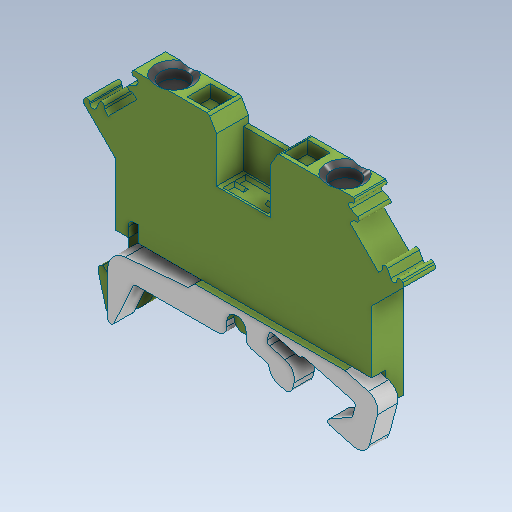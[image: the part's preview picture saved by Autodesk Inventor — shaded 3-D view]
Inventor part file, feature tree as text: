
AUTODESK INVENTOR PART (.ipt)
format: ipt  version: 2025.2 (Build 292293000, 293)  size: 846,336 bytes
history: native  units: mm
features: other x130, sketch x12, extrude x10, hole x2
ambient origin geometry x8: Origin, YZ Plane, XZ Plane, XY Plane, X Axis, Y Axis, Z Axis, Center Point
bodies: Solid1 (feature_tree)
feature tree (154):
  extrude  "Extrusion1"  Depth=2.1mm TaperAngle=0.0deg
  extrude  "Extrusion2"  Depth=2.0mm TaperAngle=0.0deg
  extrude  "Extrusion3"  Depth=7.0mm TaperAngle=0.0deg
  extrude  "Extrusion4"  Depth=5.0mm TaperAngle=0.0deg
  extrude  "Extrusion5"  Depth=3.6mm TaperAngle=0.0deg
  extrude  "Extrusion6"  TaperAngle=0.0deg  [1 undecoded]
  extrude  "Extrusion7"  TaperAngle=0.0deg  [1 undecoded]
  extrude  "Extrusion8"  TaperAngle=0.0deg  [1 undecoded]
  hole  "Hole1"  [1 undecoded]
  hole  "Hole2"  [1 undecoded]
  extrude  "Extrusion9"  Depth=10.0mm
  extrude  "Extrusion10"  Depth=10.0mm
  other  "1_2_XY"
  other  "1_2_YZ"
  other  "1_2_ZX"
  other  "1_2_X"
  other  "1_2_Y"
  other  "1_2_Z"
  other  "1_2_Center"
  other  "1_3_XY"
  other  "1_3_YZ"
  other  "1_3_ZX"
  other  "1_3_X"
  other  "1_3_Y"
  other  "1_3_Z"
  other  "1_3_Center"
  other  "1_4_XY"
  other  "1_4_YZ"
  other  "1_4_ZX"
  other  "1_4_X"
  other  "1_4_Y"
  other  "1_4_Z"
  other  "1_4_Center"
  other  "1_5_XY"
  other  "1_5_YZ"
  other  "1_5_ZX"
  other  "1_5_X"
  other  "1_5_Y"
  other  "1_5_Z"
  other  "1_5_Center"
  other  "1_6_XY"
  other  "1_6_YZ"
  other  "1_6_ZX"
  other  "1_6_X"
  other  "1_6_Y"
  other  "1_6_Z"
  other  "1_6_Center"
  other  "1_7_XY"
  other  "1_7_YZ"
  other  "1_7_ZX"
  other  "1_7_X"
  other  "1_7_Y"
  other  "1_7_Z"
  other  "1_7_Center"
  other  "1_8_XY"
  other  "1_8_YZ"
  other  "1_8_ZX"
  other  "1_8_X"
  other  "1_8_Y"
  other  "1_8_Z"
  other  "1_8_Center"
  other  "MD_XY"
  other  "MD_YZ"
  other  "MD_ZX"
  other  "MD_X"
  other  "MD_Y"
  other  "MD_Z"
  other  "MD_Center"
  other  "OP_XY"
  other  "OP_YZ"
  other  "OP_ZX"
  other  "OP_X"
  other  "OP_Y"
  other  "OP_Z"
  other  "OP_Center"
  other  "a1_XY"
  other  "a1_YZ"
  other  "a1_ZX"
  other  "a1_X"
  other  "a1_Y"
  other  "a1_Z"
  other  "a1_Center"
  other  "b2_XY"
  other  "b2_YZ"
  other  "b2_ZX"
  other  "b2_X"
  other  "b2_Y"
  other  "b2_Z"
  other  "b2_Center"
  other  "j3_XY"
  other  "j3_YZ"
  other  "j3_ZX"
  other  "j3_X"
  other  "j3_Y"
  other  "j3_Z"
  other  "j3_Center"
  other  "m4_XY"
  other  "m4_YZ"
  other  "m4_ZX"
  other  "m4_X"
  other  "m4_Y"
  other  "m4_Z"
  other  "m4_Center"
  other  "m5_XY"
  other  "m5_YZ"
  other  "m5_ZX"
  other  "m5_X"
  other  "m5_Y"
  other  "m5_Z"
  other  "m5_Center"
  other  "z6_XY"
  other  "z6_YZ"
  other  "z6_ZX"
  other  "z6_X"
  other  "z6_Y"
  other  "z6_Z"
  other  "z6_Center"
  other  "z7_XY"
  other  "z7_YZ"
  other  "z7_ZX"
  other  "z7_X"
  other  "z7_Y"
  other  "z7_Z"
  other  "z7_Center"
  other  "Edição direta1"
  other  "Edição direta2"
  other  "Edição direta3"
  other  "Edição direta4"
  other  "Edição direta5"
  other  "Edição direta6"
  other  "Edição direta7"
  other  "Edição direta8"
  other  "Edição direta9"
  sketch  "Skizze_1"  dims[d0=5.0mm d1=0.0mm d2=2.1mm d3=0.0mm]
  sketch  "Skizze_14"  dims[d39=0.0mm d40=0.0mm]
  sketch  "Skizze_15"  dims[d41=3.0mm d42=10.0mm d43=10.0mm d44=12.3mm d45=10.0mm d46=10.0mm]
  sketch  "Skizze_16"  dims[d47=12.0mm d48=10.0mm d49=10.0mm d50=0.25mm d51=0.55mm d52=-0.36mm d53=-0.4mm d54=0.0mm d55=0.0mm d56=0.0mm d57=0.0mm d58=0.35mm d59=0.5mm]
  sketch  "Skizze_2"  dims[d4=2.1mm d5=0.0mm d6=2.0mm d7=0.0mm]
  sketch  "Skizze_3"  dims[d8=0.8mm d9=0.0mm d10=7.0mm d11=0.0mm]
  sketch  "Skizze_4"  dims[d12=3.4mm d13=0.0mm d14=5.0mm d15=0.0mm]
  sketch  "Skizze_5"  dims[d16=4.2mm d17=6.0mm d18=5.8mm d19=2.0mm d20=18.545904mm d21=2.0mm d22=0.0mm]
  sketch  "Sketch9"  dims[d32=3.6mm d33=0.0mm d34=0.0mm]
  sketch  "Sketch10"  dims[d37=0.0mm d38=0.0mm]
  sketch  "Skizze_8"  dims[d23=4.2mm d24=6.0mm d25=5.8mm d26=2.0mm d27=18.545904mm d28=2.0mm d29=0.0mm d30=3.6mm d31=0.0mm]
  sketch  "Skizze_9"  dims[d35=0.0mm d36=0.0mm]
  other  "Escala1"
  other  "Escala2"
  other  "Escala3"
  other  "Tamanho1"
  other  "Tamanho2"
  other  "Tamanho3"
  other  "Mover1"
  other  "Mover2"
  other  "Tamanho4"
note: 5 required parameter values undecoded (feature->parameter linkage not recoverable at this tier; creation-order binding heuristic only, values carry confidence <= 0.55)
